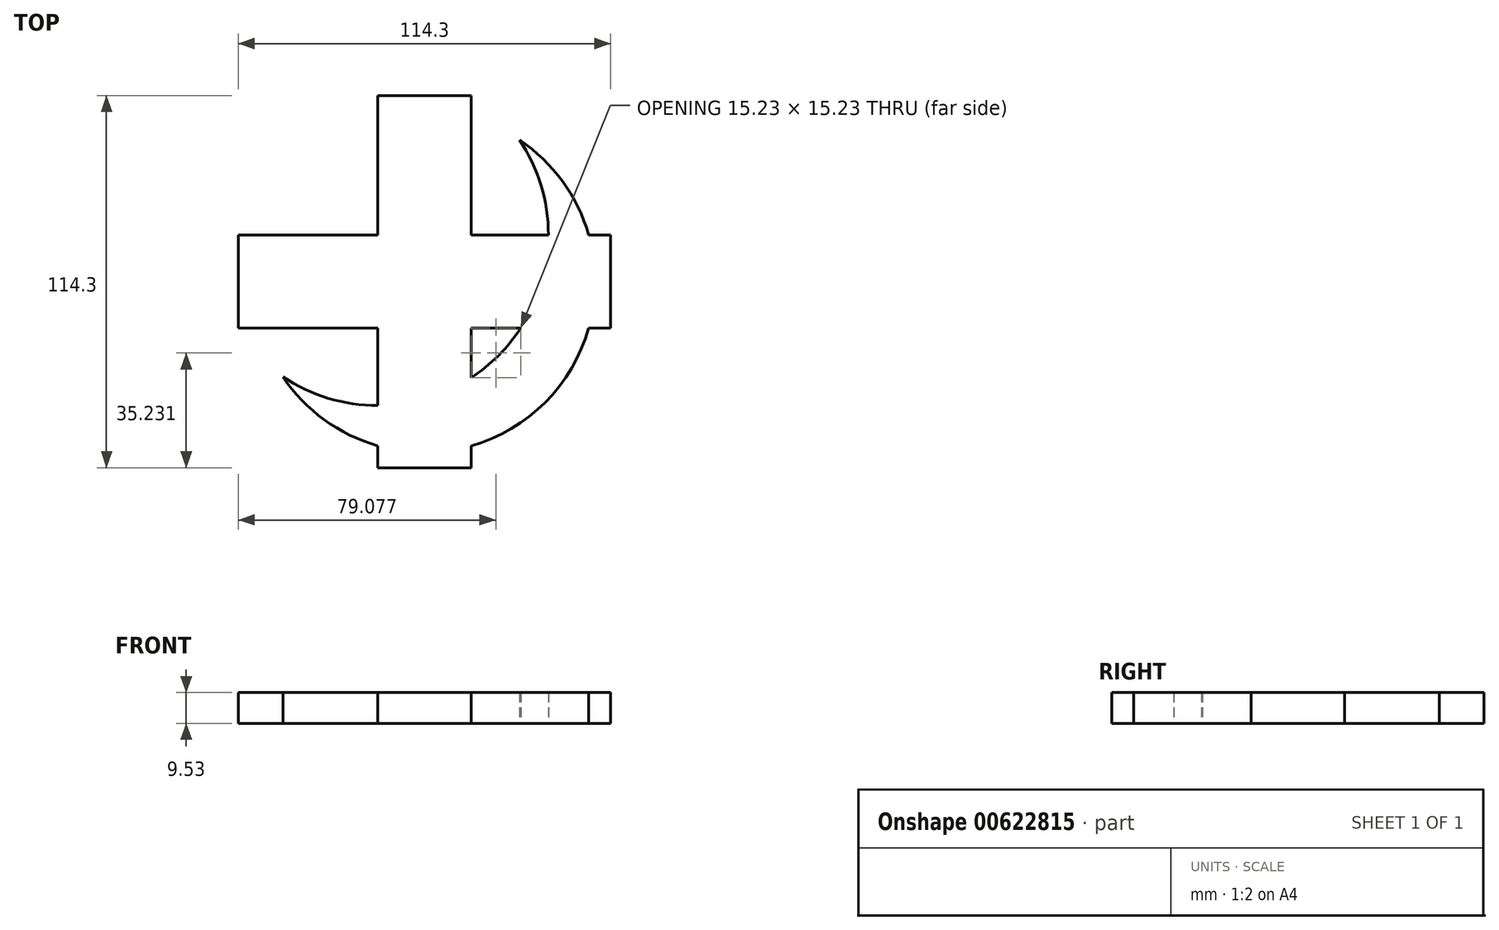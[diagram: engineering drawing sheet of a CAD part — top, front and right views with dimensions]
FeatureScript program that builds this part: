
annotation { "Feature Type Name" : "Feature", "Feature Type Description" : "" }
export const myFeature = defineFeature(function(context is Context, id is Id, definition is map)
    precondition{}
    {
        {
            var Q0;
            Q0=qCreatedBy(makeId("Top.planeOp"),FACE);
            var sketch = newSketch(context, id + "F0", { "sketchPlane" : qUnion([Q0])});
            skPoint(sketch, "E0", {"position": v(-6.92, -47.75) * mm});
            skArc(sketch, "E1", {"start": v(-50.37, -19.84) * mm, "mid": v(-36.47, -26.4) * mm, "end": v(-21.26, -28.66) * mm});
            skArc(sketch, "E2", {"start": v(-50.37, -19.84) * mm, "mid": v(-37.7, -33) * mm, "end": v(-21.26, -41) * mm});
            skLineSegment(sketch, "E3", {"start": v(-21.24, 23.7) * mm, "end": v(-64.07, 23.7) * mm});
            skLineSegment(sketch, "E4", {"start": v(-64.07, 23.7) * mm, "end": v(-64.07, -4.9) * mm});
            skLineSegment(sketch, "E5", {"start": v(-64.07, -4.9) * mm, "end": v(-21.26, -4.9) * mm});
            skLineSegment(sketch, "E6", {"start": v(-21.26, -4.9) * mm, "end": v(-21.26, -28.66) * mm});
            skLineSegment(sketch, "E7", {"start": v(-21.26, -47.75) * mm, "end": v(7.4, -47.75) * mm});
            skLineSegment(sketch, "E8", {"start": v(7.4, -47.75) * mm, "end": v(7.4, -41.02) * mm});
            skLineSegment(sketch, "E9", {"start": v(7.4, -4.9) * mm, "end": v(22.62, -4.9) * mm});
            skLineSegment(sketch, "E10", {"start": v(50.23, -4.9) * mm, "end": v(50.23, 23.75) * mm});
            skLineSegment(sketch, "E11", {"start": v(7.4, 23.75) * mm, "end": v(7.4, 66.55) * mm});
            skLineSegment(sketch, "E12", {"start": v(7.4, 66.55) * mm, "end": v(-21.26, 66.55) * mm});
            skLineSegment(sketch, "E13", {"start": v(-21.26, 66.55) * mm, "end": v(-21.24, 23.7) * mm});
            skArc(sketch, "E14.trimOffspring", {"start": v(7.4, -20.13) * mm, "mid": v(15.8, -13.3) * mm, "end": v(22.62, -4.9) * mm});
            skLineSegment(sketch, "E15.trimOffspring", {"start": v(-21.26, -41) * mm, "end": v(-21.26, -47.75) * mm});
            skArc(sketch, "E16.trimOffspring", {"start": v(7.4, -41.02) * mm, "mid": v(30.15, -27.66) * mm, "end": v(43.51, -4.9) * mm});
            skLineSegment(sketch, "E17.trimOffspring", {"start": v(7.4, -20.13) * mm, "end": v(7.4, -4.9) * mm});
            skLineSegment(sketch, "E18.trimOffspring", {"start": v(43.51, -4.9) * mm, "end": v(50.23, -4.9) * mm});
            skArc(sketch, "E19.trimOffspring", {"start": v(31.15, 23.75) * mm, "mid": v(28.9, 38.97) * mm, "end": v(22.31, 52.88) * mm});
            skArc(sketch, "E20.trimOffspring", {"start": v(43.49, 23.75) * mm, "mid": v(35.48, 40.2) * mm, "end": v(22.31, 52.88) * mm});
            skLineSegment(sketch, "E21.trimOffspring", {"start": v(31.15, 23.75) * mm, "end": v(7.4, 23.75) * mm});
            skLineSegment(sketch, "E22", {"start": v(43.49, 23.75) * mm, "end": v(50.23, 23.75) * mm});
            skSolve(sketch);
        }
        {
            var Q0;
            Q0=makeQuery(id+"F0.imprint","IMPRINT",FACE,{"disambiguationData":[TD([[makeQuery(id+"F0.imprint","IMPRINT",EDGE,{"derivedFrom":sQuery(id+"F0.wireOp",EDGE,"E1")}),-1.0]])]});
            extrude(context, id + "F1", {"entities" : qUnion([Q0]), "depth" : 9.52 * mm, "offsetDistance" : 25.4 * mm});
        }
    });
